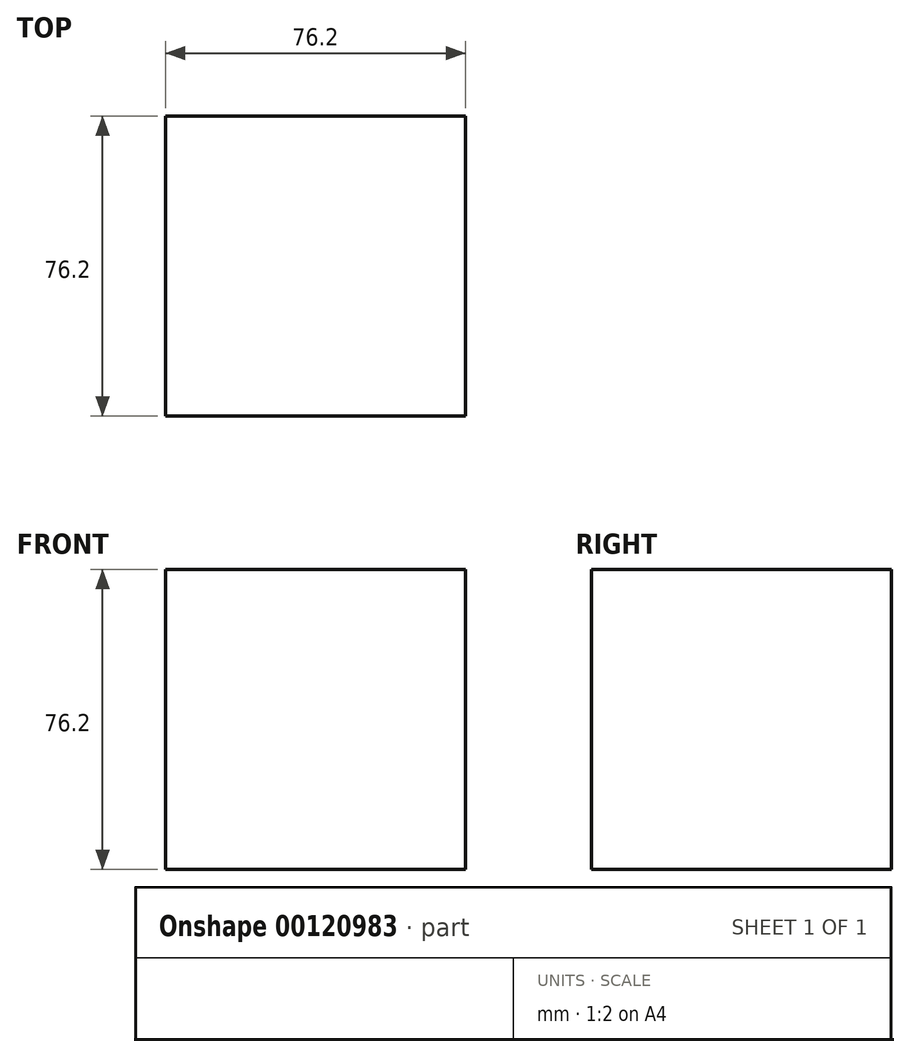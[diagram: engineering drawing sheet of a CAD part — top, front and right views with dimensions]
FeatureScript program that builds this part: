
annotation { "Feature Type Name" : "Feature", "Feature Type Description" : "" }
export const myFeature = defineFeature(function(context is Context, id is Id, definition is map)
    precondition{}
    {
        {
            var Q0;
            Q0=qCreatedBy(makeId("Top.planeOp"),FACE);
            var sketch = newSketch(context, id + "F0", { "sketchPlane" : qUnion([Q0])});
            skLineSegment(sketch, "E0.bottom", {"start": v(-38.1, -38.1) * mm, "end": v(38.1, -38.1) * mm});
            skLineSegment(sketch, "E0.top", {"start": v(-38.1, 38.1) * mm, "end": v(38.1, 38.1) * mm});
            skLineSegment(sketch, "E0.left", {"start": v(-38.1, -38.1) * mm, "end": v(-38.1, 38.1) * mm});
            skLineSegment(sketch, "E0.right", {"start": v(38.1, -38.1) * mm, "end": v(38.1, 38.1) * mm});
            skPoint(sketch, "E0.middle", {"position": v(0, 0) * mm});
            skSolve(sketch);
        }
        {
            var Q0;
            Q0 = qSketchRegion(id + "F0", true);
            extrude(context, id + "F1", {"entities" : qUnion([Q0]), "depth" : 76.2 * mm});
        }
    });
